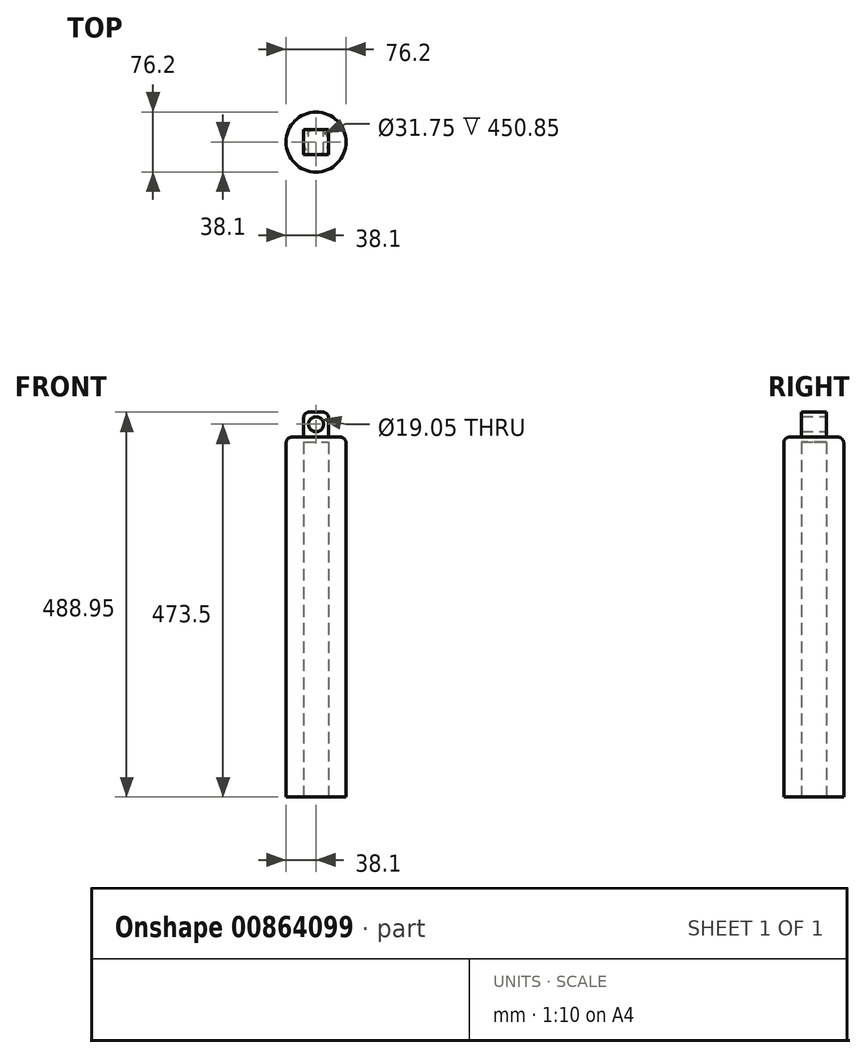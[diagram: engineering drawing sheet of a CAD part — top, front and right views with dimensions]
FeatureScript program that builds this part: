
annotation { "Feature Type Name" : "Feature", "Feature Type Description" : "" }
export const myFeature = defineFeature(function(context is Context, id is Id, definition is map)
    precondition{}
    {
        {
            var Q0;
            Q0=qCreatedBy(makeId("Top.planeOp"),FACE);
            var sketch = newSketch(context, id + "F0", { "sketchPlane" : qUnion([Q0])});
            skCircle(sketch, "E0", {"center": v(0, 0) * mm, "radius": 38.1 * mm});
            skSolve(sketch);
        }
        {
            var Q0;
            Q0=makeQuery(id+"F0.imprint","IMPRINT",FACE,{"disambiguationData":[TD([[makeQuery(id+"F0.imprint","IMPRINT",EDGE,{"derivedFrom":sQuery(id+"F0.wireOp",EDGE,"E0")}),1.0]])]});
            extrude(context, id + "F1", {"entities" : qUnion([Q0]), "oppositeDirection" : true, "depth" : 457.2 * mm, "offsetDistance" : 25.4 * mm});
        }
        {
            var Q0;
            Q0=qCreatedBy(makeId("Front.planeOp"),FACE);
            var sketch = newSketch(context, id + "F2", { "sketchPlane" : qUnion([Q0])});
            skLineSegment(sketch, "E1.bottom", {"start": v(15.88, -31.75) * mm, "end": v(-15.88, -31.75) * mm});
            skLineSegment(sketch, "E1.top", {"start": v(15.88, 31.75) * mm, "end": v(-15.87, 31.75) * mm});
            skLineSegment(sketch, "E1.left", {"start": v(15.88, -31.75) * mm, "end": v(15.88, 31.75) * mm});
            skLineSegment(sketch, "E1.right", {"start": v(-15.88, -31.75) * mm, "end": v(-15.87, 31.75) * mm});
            skPoint(sketch, "E1.middle", {"position": v(0, 0) * mm});
            skCircle(sketch, "E2", {"center": v(0, 16.3) * mm, "radius": 9.53 * mm});
            skSolve(sketch);
        }
        {
            var Q0;
            Q0=makeQuery(id+"F2.imprint","IMPRINT",FACE,{"disambiguationData":[TD([[makeQuery(id+"F2.imprint","IMPRINT",EDGE,{"derivedFrom":sQuery(id+"F2.wireOp",EDGE,"E1.bottom")}),-1.0]])]});
            extrude(context, id + "F3", {"entities" : qUnion([Q0]), "operationType" : NewBodyOperationType.ADD, "depth" : 31.75 * mm, "offsetDistance" : 25.4 * mm, "symmetric" : true});
        }
        {
            var Q0;
            Q0=makeQuery(id+"F3.opExtrude","SWEPT_EDGE",EDGE,{"disambiguationData":[OSD([sQuery(id+"F2.wireOp",EDGE,"E1.top"),sQuery(id+"F2.wireOp",EDGE,"E1.left")])]});
            var Q1;
            Q1=makeQuery(id+"F3.opExtrude","SWEPT_EDGE",EDGE,{"disambiguationData":[OSD([sQuery(id+"F2.wireOp",EDGE,"E1.top"),sQuery(id+"F2.wireOp",EDGE,"E1.right")])]});
            var Q2;
            Q2=makeQuery(id+"F1.opExtrude","CAP_EDGE",EDGE,{"disambiguationData":[OSD([sQuery(id+"F0.wireOp",EDGE,"E0")])],"isStart":true});
            fillet(context, id + "F4", {"entities" : qUnion([Q0, Q1, Q2]), "radius" : 7.62 * mm, "tangentPropagation" : true, "allowEdgeOverflow" : false});
        }
        {
            var Q0;
            Q0=makeQuery(id+"F1.opExtrude","CAP_FACE",FACE,{"disambiguationData":[OSD([sQuery(id+"F0.wireOp",EDGE,"E0")])],"isStart":false});
            var sketch = newSketch(context, id + "F5", { "sketchPlane" : qUnion([Q0])});
            skCircle(sketch, "E3", {"center": v(0, 0) * mm, "radius": 15.88 * mm});
            skSolve(sketch);
        }
        {
            var Q0;
            Q0=makeQuery(id+"F5.imprint","IMPRINT",FACE,{"disambiguationData":[TD([[makeQuery(id+"F5.imprint","IMPRINT",EDGE,{"derivedFrom":sQuery(id+"F5.wireOp",EDGE,"E3")}),1.0]])]});
            extrude(context, id + "F6", {"entities" : qUnion([Q0]), "operationType" : NewBodyOperationType.REMOVE, "oppositeDirection" : true, "depth" : 450.85 * mm, "offsetDistance" : 25.4 * mm});
        }
    });
